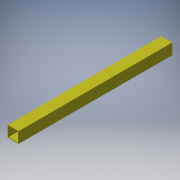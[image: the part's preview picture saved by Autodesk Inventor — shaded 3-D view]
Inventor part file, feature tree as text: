
AUTODESK INVENTOR PART (.ipt)
format: ipt  version: 2017 SP1 (Build 210196100, 196)  size: 98,816 bytes
history: native  units: in
note: dims shown in document units (in); Inventor stores cm internally (conversion verified against a paired STEP export)
features: extrude x1, sketch x1
ambient origin geometry x8: Origin, YZ Plane, XZ Plane, XY Plane, X Axis, Y Axis, Z Axis, Center Point
bodies: Solid1 (feature_tree)
feature tree (2):
  extrude  "Extrusion1"  Depth=1.0in
  sketch  "Sketch1"  dims[d0=1.0in d1=1.0in d2=0.0625in d3=14.0in d4=0.0in]
